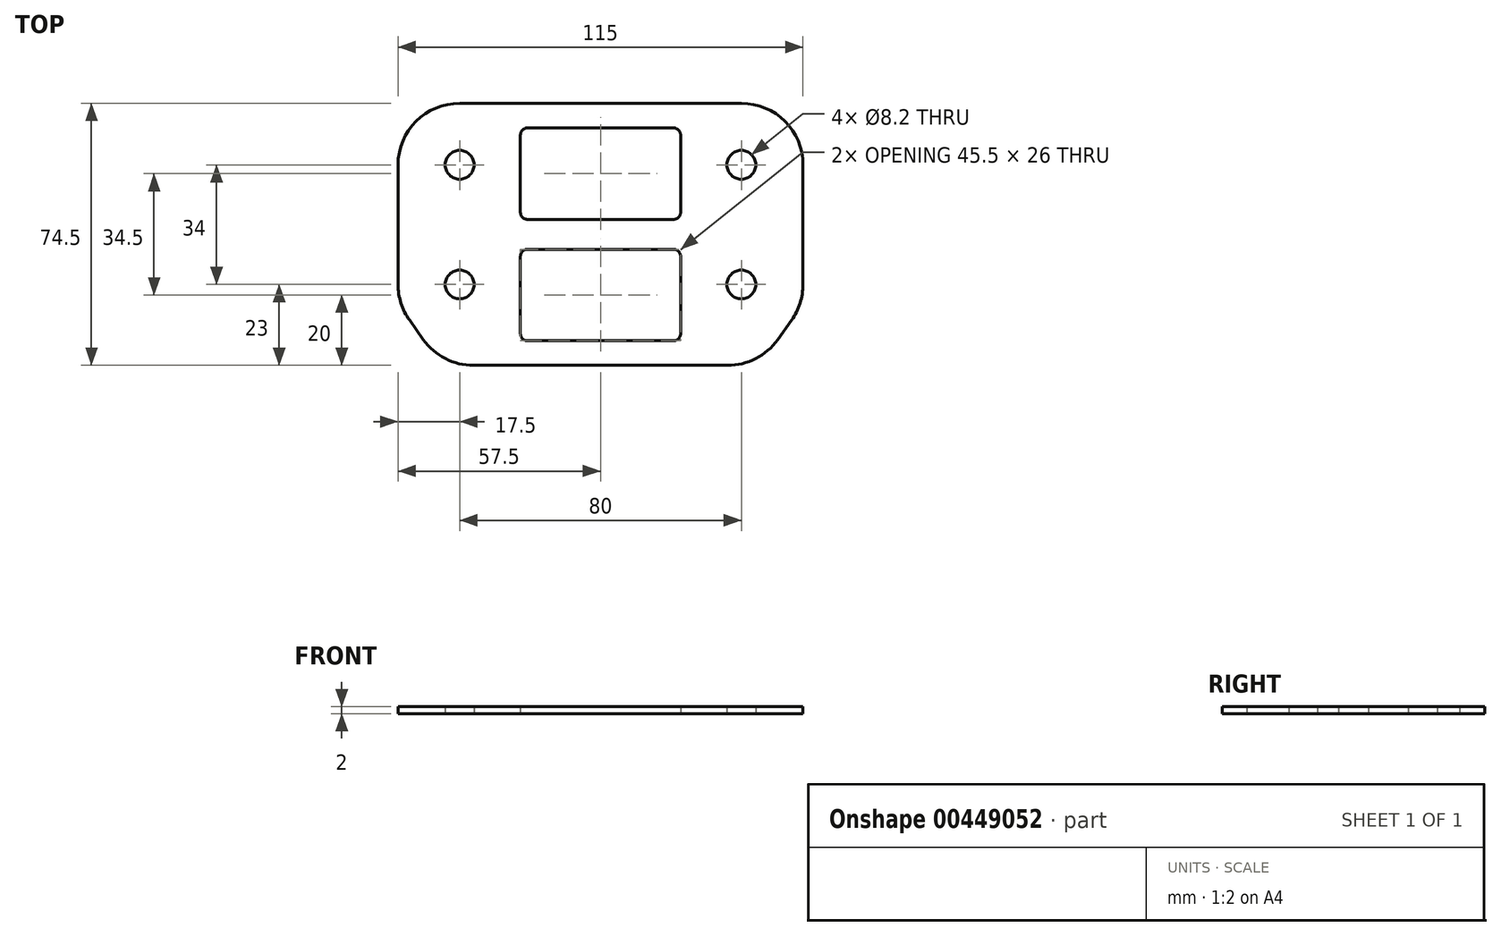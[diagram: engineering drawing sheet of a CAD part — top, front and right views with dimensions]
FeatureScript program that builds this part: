
annotation { "Feature Type Name" : "Feature", "Feature Type Description" : "" }
export const myFeature = defineFeature(function(context is Context, id is Id, definition is map)
    precondition{}
    {
        {
            var Q0;
            Q0=qCreatedBy(makeId("Top.planeOp"),FACE);
            var sketch = newSketch(context, id + "F0", { "sketchPlane" : qUnion([Q0])});
            skCircle(sketch, "E0", {"center": v(-40, 17) * mm, "radius": 12.5 * mm});
            skCircle(sketch, "E1", {"center": v(-40, -17) * mm, "radius": 12.5 * mm});
            skLineSegment(sketch, "E2.bottom", {"start": v(-22.75, 27.5) * mm, "end": v(0, 27.5) * mm});
            skLineSegment(sketch, "E2.top", {"start": v(-22.75, 1.5) * mm, "end": v(0, 1.5) * mm});
            skLineSegment(sketch, "E2.left", {"start": v(-22.75, 27.5) * mm, "end": v(-22.75, 1.5) * mm});
            skArc(sketch, "E3", {"start": v(-57.5, -17) * mm, "mid": v(-56.66, -22.34) * mm, "end": v(-54.24, -27.18) * mm});
            skLineSegment(sketch, "E4", {"start": v(-40, 34.5) * mm, "end": v(0, 34.5) * mm});
            skLineSegment(sketch, "E5.MirrorCS", {"start": v(-22.75, -33) * mm, "end": v(0, -33) * mm});
            skLineSegment(sketch, "E6.MirrorCS", {"start": v(-22.75, -33) * mm, "end": v(-22.75, -7) * mm});
            skLineSegment(sketch, "E7.0", {"start": v(-22.75, -7) * mm, "end": v(0, -7) * mm});
            skLineSegment(sketch, "E8", {"start": v(-36.07, -40) * mm, "end": v(0, -40) * mm});
            skLineSegment(sketch, "E9", {"start": v(-54.24, -27.18) * mm, "end": v(-50.3, -32.68) * mm});
            skArc(sketch, "E10.filletArc", {"start": v(-50.3, -32.68) * mm, "mid": v(-44.07, -38.06) * mm, "end": v(-36.07, -40) * mm});
            skLineSegment(sketch, "E11", {"start": v(-57.5, 17) * mm, "end": v(-57.5, -17) * mm});
            skLineSegment(sketch, "E12", {"start": v(0, 34.5) * mm, "end": v(0, -40) * mm});
            skArc(sketch, "E13.trimOffspring", {"start": v(-40, 34.5) * mm, "mid": v(-52.37, 29.37) * mm, "end": v(-57.5, 17) * mm});
            skPoint(sketch, "E14.orphan", {"position": v(0, 48.45) * mm});
            skSolve(sketch);
        }
        {
            var Q0;
            Q0 = qSketchRegion(id + "F0", true);
            var Q1;
            Q1=makeQuery(id+"F0.imprint","IMPRINT",FACE,{"disambiguationData":[TD([[makeQuery(id+"F0.imprint","IMPRINT",EDGE,{"derivedFrom":sQuery(id+"F0.wireOp",EDGE,"E0")}),1.0]])]});
            var Q2;
            Q2=makeQuery(id+"F0.imprint","IMPRINT",FACE,{"disambiguationData":[TD([[makeQuery(id+"F0.imprint","IMPRINT",EDGE,{"derivedFrom":sQuery(id+"F0.wireOp",EDGE,"E1")}),1.0]])]});
            var Q3;
            {var subQ0=sQuery(id+"F0.wireOp",EDGE,"9J0quNDy-q7js-6mQw-9BaX-7pUd6Maq4VlN");Q3=makeQuery(id+"F0.imprint","IMPRINT",FACE,{"disambiguationData":[TD([[makeQuery(id+"F0.imprint","IMPRINT",EDGE,{"derivedFrom":subQ0}),1.0]])]});}
            extrude(context, id + "F1", {"entities" : qUnion([Q0, Q1, Q2, Q3]), "depth" : 2 * mm});
        }
        {
            var Q0;
            {var subQ0=sQuery(id+"F0.wireOp",EDGE,"E2.bottom");Q0=makeQuery(id+"F0.imprint","IMPRINT",FACE,{"disambiguationData":[TD([[makeQuery(id+"F0.imprint","IMPRINT",EDGE,{"derivedFrom":subQ0}),-1.0]])]});}
            var Q1;
            {var subQ0=sQuery(id+"F0.wireOp",EDGE,"E5.MirrorCS");Q1=makeQuery(id+"F0.imprint","IMPRINT",FACE,{"disambiguationData":[TD([[makeQuery(id+"F0.imprint","IMPRINT",EDGE,{"derivedFrom":subQ0}),1.0]])]});}
            extrude(context, id + "F2", {"entities" : qUnion([Q0, Q1]), "operationType" : NewBodyOperationType.REMOVE, "depth" : 25 * mm});
        }
        {
            var Q0;
            Q0=makeQuery(id+"F2.boolean.opBoolean","COPY",EDGE,{"derivedFrom":makeQuery(id+"F2.opExtrude","SWEPT_EDGE",EDGE,{"disambiguationData":[OSD([sQuery(id+"F0.wireOp",EDGE,"E2.top"),sQuery(id+"F0.wireOp",EDGE,"E2.left")])]})});
            var Q1;
            Q1=makeQuery(id+"F2.boolean.opBoolean","COPY",EDGE,{"derivedFrom":makeQuery(id+"F2.opExtrude","SWEPT_EDGE",EDGE,{"disambiguationData":[OSD([sQuery(id+"F0.wireOp",EDGE,"E2.bottom"),sQuery(id+"F0.wireOp",EDGE,"E2.left")])]})});
            var Q2;
            Q2=makeQuery(id+"F2.boolean.opBoolean","COPY",EDGE,{"derivedFrom":makeQuery(id+"F2.opExtrude","SWEPT_EDGE",EDGE,{"disambiguationData":[OSD([sQuery(id+"F0.wireOp",EDGE,"E6.MirrorCS"),sQuery(id+"F0.wireOp",EDGE,"E7.0")])]})});
            var Q3;
            Q3=makeQuery(id+"F2.boolean.opBoolean","COPY",EDGE,{"derivedFrom":makeQuery(id+"F2.opExtrude","SWEPT_EDGE",EDGE,{"disambiguationData":[OSD([sQuery(id+"F0.wireOp",EDGE,"E5.MirrorCS"),sQuery(id+"F0.wireOp",EDGE,"E6.MirrorCS")])]})});
            fillet(context, id + "F3", {"entities" : qUnion([Q0, Q1, Q2, Q3]), "radius" : 2 * mm, "tangentPropagation" : true, "allowEdgeOverflow" : false});
        }
        {
            var Q0;
            Q0=sQuery(id+"F0.wireOp",VERTEX,"E0.center");
            var Q1;
            Q1=sQuery(id+"F0.wireOp",VERTEX,"E1.center");
            var Q2;
            Q2=makeQuery(id+"F1.opExtrude","SWEPT_BODY",BODY,{"disambiguationData":[OSD([sQuery(id+"F0.wireOp",EDGE,"E3"),sQuery(id+"F0.wireOp",EDGE,"E4"),sQuery(id+"F0.wireOp",EDGE,"E8"),sQuery(id+"F0.wireOp",EDGE,"E9"),sQuery(id+"F0.wireOp",EDGE,"E10.filletArc"),sQuery(id+"F0.wireOp",EDGE,"E11"),sQuery(id+"F0.wireOp",EDGE,"E12"),sQuery(id+"F0.wireOp",EDGE,"E13.trimOffspring")])]});
            hole(context, id + "F4", {"style" : HoleStyle.SIMPLE, "endStyle" : HoleEndStyle.THROUGH, "oppositeDirection" : true, "holeDiameter" : 8.2 * mm, "isTappedThrough" : true, "tappedDepth" : 12 * mm, "tapClearance" : 3, "locations" : qUnion([Q0, Q1]), "scope" : qUnion([Q2])});
        }
        {
            var Q0;
            Q0=makeQuery(id+"F1.opExtrude","SWEPT_BODY",BODY,{"disambiguationData":[OSD([sQuery(id+"F0.wireOp",EDGE,"E3"),sQuery(id+"F0.wireOp",EDGE,"E4"),sQuery(id+"F0.wireOp",EDGE,"E8"),sQuery(id+"F0.wireOp",EDGE,"E9"),sQuery(id+"F0.wireOp",EDGE,"E10.filletArc"),sQuery(id+"F0.wireOp",EDGE,"E11"),sQuery(id+"F0.wireOp",EDGE,"E12"),sQuery(id+"F0.wireOp",EDGE,"E13.trimOffspring")])]});
            var Q1;
            Q1=qCreatedBy(makeId("Right.planeOp"),FACE);
            mirror(context, id + "F5", {"operationType" : NewBodyOperationType.ADD, "entities" : qUnion([Q0]), "mirrorPlane" : qUnion([Q1])});
        }
    });
